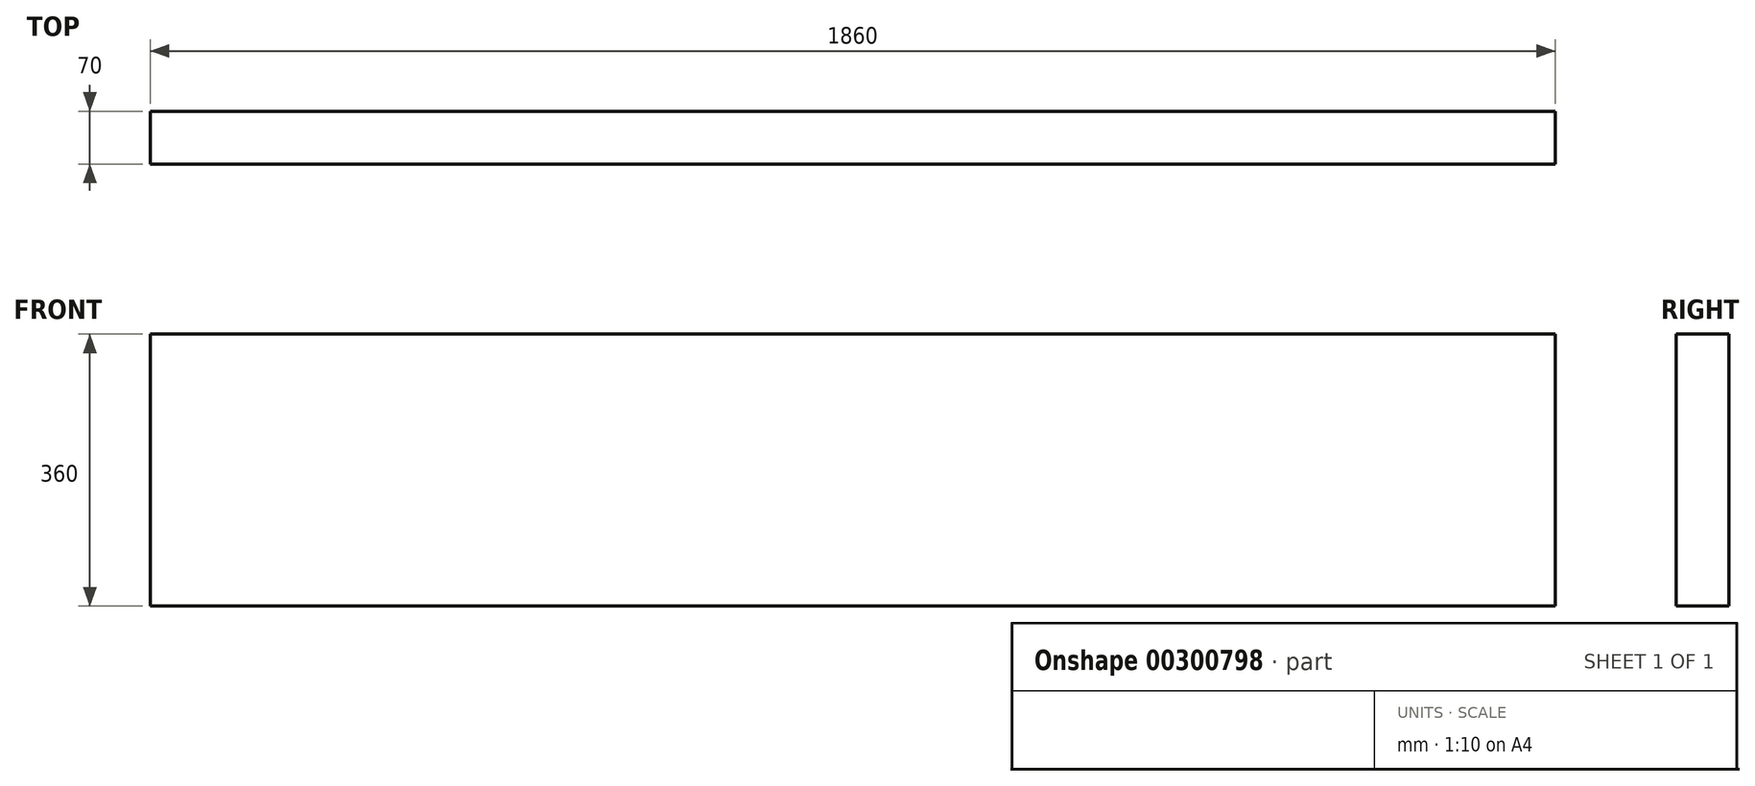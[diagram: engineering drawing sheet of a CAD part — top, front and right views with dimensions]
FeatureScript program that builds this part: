
annotation { "Feature Type Name" : "Feature", "Feature Type Description" : "" }
export const myFeature = defineFeature(function(context is Context, id is Id, definition is map)
    precondition{}
    {
        {
            var Q0;
            Q0=qCreatedBy(makeId("Front.planeOp"),FACE);
            var sketch = newSketch(context, id + "F0", { "sketchPlane" : qUnion([Q0])});
            skLineSegment(sketch, "E0.bottom", {"start": v(-918.71, -213.6) * mm, "end": v(941.29, -213.6) * mm});
            skLineSegment(sketch, "E0.top", {"start": v(-918.71, -573.6) * mm, "end": v(941.29, -573.6) * mm});
            skLineSegment(sketch, "E0.left", {"start": v(-918.71, -213.6) * mm, "end": v(-918.71, -573.6) * mm});
            skLineSegment(sketch, "E0.right", {"start": v(941.29, -213.6) * mm, "end": v(941.29, -573.6) * mm});
            skSolve(sketch);
        }
        {
            var Q0;
            Q0=makeQuery(id+"F0.imprint","IMPRINT",FACE,{"disambiguationData":[TD([[makeQuery(id+"F0.imprint","IMPRINT",EDGE,{"derivedFrom":sQuery(id+"F0.wireOp",EDGE,"E0.bottom")}),-1.0]])]});
            extrude(context, id + "F1", {"entities" : qUnion([Q0]), "depth" : 70 * mm});
        }
    });
